FCSTD DOCUMENT  (FreeCAD 0.16R6712 (Git))
Label: UP Dose Halter
License: All rights reserved
LicenseURL: http://en.wikipedia.org/wiki/All_rights_reserved
objects: Sketcher::SketchObject×1
note: 1 computed .brp shape members not serialized (recipe doc carries the construction recipe); baked Part::Feature solids carry a one-line shape summary decoded from their .brp

FEATURE [Sketcher::SketchObject] Sketch
  sketch-geometry (39):
    g0: LineSegment StartX=7.03221 StartY=75.7575 StartZ=0 EndX=7.03221 EndY=69.7575 EndZ=0
    g1: LineSegment [constr] StartX=15.0322 StartY=67.7575 StartZ=0 EndX=15.0322 EndY=42.7575 EndZ=0
    g2: ArcOfCircle CenterX=15.0322 CenterY=42.7575 CenterZ=0 NormalX=0 NormalY=0 NormalZ=1 Radius=32 StartAngle=1.47063 EndAngle=1.67096
    g3: ArcOfCircle CenterX=15.0322 CenterY=42.7575 CenterZ=0 NormalX=0 NormalY=0 NormalZ=1 Radius=28 StartAngle=1.47063 EndAngle=1.67096
    g4: ArcOfCircle CenterX=18.0322 CenterY=72.6071 CenterZ=0 NormalX=0 NormalY=0 NormalZ=1 Radius=2 StartAngle=4.61222 EndAngle=7.75382
    g5: ArcOfCircle CenterX=12.0322 CenterY=72.6071 CenterZ=0 NormalX=0 NormalY=0 NormalZ=1 Radius=2 StartAngle=1.67096 EndAngle=4.81256
    g6: LineSegment [constr] StartX=18.0322 StartY=65.7575 StartZ=0 EndX=18.0322 EndY=72.6071 EndZ=0
    g7: ArcOfCircle CenterX=15.0322 CenterY=42.7575 CenterZ=0 NormalX=0 NormalY=0 NormalZ=1 Radius=32 StartAngle=4.61222 EndAngle=4.81256
    g8: ArcOfCircle CenterX=15.0322 CenterY=42.7575 CenterZ=0 NormalX=0 NormalY=0 NormalZ=1 Radius=28 StartAngle=4.61222 EndAngle=4.81256
    g9: ArcOfCircle CenterX=12.0322 CenterY=12.9079 CenterZ=0 NormalX=0 NormalY=0 NormalZ=1 Radius=2 StartAngle=1.47063 EndAngle=4.61222
    g10: ArcOfCircle CenterX=18.0322 CenterY=12.9079 CenterZ=0 NormalX=0 NormalY=0 NormalZ=1 Radius=2 StartAngle=4.81255 EndAngle=7.95415
    g11: ArcOfCircle CenterX=21.0322 CenterY=15.7575 CenterZ=0 NormalX=0 NormalY=0 NormalZ=1 Radius=2 StartAngle=6.28318 EndAngle=7.85398
    g12: LineSegment StartX=23.0322 StartY=15.7575 StartZ=0 EndX=23.0322 EndY=9.75753 EndZ=0
    g13: ArcOfCircle CenterX=21.0322 CenterY=9.75752 CenterZ=0 NormalX=0 NormalY=0 NormalZ=1 Radius=2 StartAngle=4.71239 EndAngle=6.28319
    g14: LineSegment StartX=7.03221 StartY=15.7575 StartZ=0 EndX=7.03221 EndY=9.75753 EndZ=0
    g15: ArcOfCircle CenterX=9.03221 CenterY=9.75752 CenterZ=0 NormalX=0 NormalY=0 NormalZ=1 Radius=2 StartAngle=3.14159 EndAngle=4.71239
    g16: LineSegment StartX=9.03221 StartY=7.75752 StartZ=0 EndX=21.0322 EndY=7.75752 EndZ=0
    g17: ArcOfCircle CenterX=9.03221 CenterY=15.7575 CenterZ=0 NormalX=0 NormalY=0 NormalZ=1 Radius=2 StartAngle=1.5708 EndAngle=3.14159
    g18: LineSegment StartX=12.0322 StartY=19.7575 StartZ=0 EndX=12.0322 EndY=65.7575 EndZ=0
    g19: ArcOfCircle CenterX=10.0322 CenterY=19.7575 CenterZ=0 NormalX=0 NormalY=0 NormalZ=1 Radius=2 StartAngle=4.71239 EndAngle=6.28319
    g20: LineSegment StartX=9.03221 StartY=17.7575 StartZ=0 EndX=10.0322 EndY=17.7575 EndZ=0
    g21: LineSegment StartX=18.0322 StartY=65.7575 StartZ=0 EndX=18.0322 EndY=19.7575 EndZ=0
    g22: ArcOfCircle CenterX=20.0322 CenterY=19.7575 CenterZ=0 NormalX=0 NormalY=0 NormalZ=1 Radius=2 StartAngle=3.14159 EndAngle=4.71239
    g23: LineSegment StartX=20.0322 StartY=17.7575 StartZ=0 EndX=21.0322 EndY=17.7575 EndZ=0
    g24: LineSegment [constr] StartX=18.0322 StartY=19.7575 StartZ=0 EndX=18.0322 EndY=12.9079 EndZ=0
    g25: ArcOfCircle CenterX=20.0322 CenterY=65.7575 CenterZ=0 NormalX=0 NormalY=0 NormalZ=1 Radius=2 StartAngle=1.5708 EndAngle=3.14159
    g26: ArcOfCircle CenterX=21.0322 CenterY=69.7575 CenterZ=0 NormalX=0 NormalY=0 NormalZ=1 Radius=2 StartAngle=4.71239 EndAngle=6.28319
    g27: LineSegment StartX=20.0322 StartY=67.7575 StartZ=0 EndX=21.0322 EndY=67.7575 EndZ=0
    g28: ArcOfCircle CenterX=21.0322 CenterY=75.7575 CenterZ=0 NormalX=0 NormalY=0 NormalZ=1 Radius=2 StartAngle=6.28318 EndAngle=7.85398
    g29: LineSegment StartX=23.0322 StartY=75.7575 StartZ=0 EndX=23.0322 EndY=69.7575 EndZ=0
    g30: ArcOfCircle CenterX=9.03221 CenterY=75.7575 CenterZ=0 NormalX=0 NormalY=0 NormalZ=1 Radius=2 StartAngle=1.5708 EndAngle=3.14159
    g31: LineSegment StartX=9.0322 StartY=77.7575 StartZ=0 EndX=21.0322 EndY=77.7575 EndZ=0
    g32: ArcOfCircle CenterX=9.03221 CenterY=69.7575 CenterZ=0 NormalX=0 NormalY=0 NormalZ=1 Radius=2 StartAngle=3.14159 EndAngle=4.71238
    g33: ArcOfCircle CenterX=10.0322 CenterY=65.7575 CenterZ=0 NormalX=0 NormalY=0 NormalZ=1 Radius=2 StartAngle=6.28318 EndAngle=7.85398
    g34: LineSegment StartX=9.0322 StartY=67.7575 StartZ=0 EndX=10.0322 EndY=67.7575 EndZ=0
    g35: LineSegment [constr] StartX=10.0322 StartY=67.7575 StartZ=0 EndX=15.0322 EndY=67.7575 EndZ=0
    g36: LineSegment [constr] StartX=12.0322 StartY=65.7575 StartZ=0 EndX=15.0322 EndY=65.7575 EndZ=0
    g37: Circle CenterX=15.0322 CenterY=58.7575 CenterZ=0 NormalX=0 NormalY=0 NormalZ=1 Radius=1.2
    g38: Circle CenterX=15.0322 CenterY=26.7575 CenterZ=0 NormalX=0 NormalY=0 NormalZ=1 Radius=1.2
  constraints (125):
    c: Vertical(g0)
    c: Vertical(g1)
    c: DistanceY(g1,g1) = 25
    c: Coincident(g2,g1)
    c: Radius(g2) = 32
    c: Coincident(g3,g1)
    c: Radius(g3) = 28
    c: Coincident(g4,g2)
    c: Coincident(g4,g3)
    c: Radius(g4) = 2
    c: Coincident(g5,g2)
    c: Coincident(g5,g3)
    c: Radius(g5) = 2
    c: DistanceX(g5,g4) = 6
    c: Coincident(g6,g4)
    c: Vertical(g6)
    c: Coincident(g7,g1)
    c: Radius(g8) = 28
    c: Radius(g7) = 32
    c: Coincident(g9,g8)
    c: Coincident(g9,g7)
    c: Coincident(g10,g8)
    c: Coincident(g10,g7)
    c: Radius(g10) = 2
    c: Equal(g10,g9)
    c: DistanceX(g9,g10) = 6
    c: Coincident(g8,g1)
    c: Vertical(g12)
    c: Vertical(g14)
    c: Coincident(g16,g15)
    c: Coincident(g12,g13)
    c: Tangent(g12,g13)
    c: Coincident(g11,g12)
    c: Horizontal(g16)
    c: Coincident(g16,g13)
    c: Tangent(g16,g15)
    c: Tangent(g14,g15)
    c: Coincident(g15,g14)
    c: Coincident(g17,g14)
    c: Tangent(g14,g17)
    c: Vertical(g18)
    c: Coincident(g19,g18)
    c: Coincident(g20,g17)
    c: Coincident(g20,g19)
    c: Horizontal(g20)
    c: Tangent(g19,g20)
    c: Tangent(g19,g18)
    c: Vertical(g21)
    c: Coincident(g22,g21)
    c: Tangent(g22,g21)
    c: Coincident(g23,g22)
    c: Horizontal(g23)
    c: Tangent(g23,g11)
    c: Tangent(g22,g23)
    c: Coincident(g24,g21)
    c: Coincident(g24,g10)
    c: Vertical(g24)
    c: DistanceX(g14,g12) = 16
    c: DistanceY(g13,g11) = 10
    c: Tangent(g12,g11)
    c: Coincident(g11,g23)
    c: Equal(g23,g20)
    c: Tangent(g17,g20)
    c: Radius(g17) = 2
    c: Equal(g17,g19)
    c: Equal(g17,g22)
    c: Equal(g17,g11)
    c: Equal(g17,g13)
    c: Equal(g17,g15)
    c: DistanceY(g15,g17) = 10
    c: DistanceX(g18,g21) = 6
    c: Coincident(g25,g21)
    c: Coincident(g27,g25)
    c: Coincident(g27,g26)
    c: Coincident(g29,g26)
    c: Coincident(g28,g29)
    c: Tangent(g21,g25)
    c: Tangent(g27,g25)
    c: Horizontal(g27)
    c: Tangent(g26,g27)
    c: Tangent(g29,g26)
    c: Tangent(g28,g29)
    c: Coincident(g30,g0)
    c: Coincident(g31,g30)
    c: Coincident(g31,g28)
    c: Horizontal(g31)
    c: Tangent(g30,g31)
    c: Tangent(g0,g30)
    c: Coincident(g34,g33)
    c: Coincident(g33,g18)
    c: Tangent(g18,g33)
    c: Tangent(g33,g34)
    c: Tangent(g32,g34)
    c: Tangent(g0,g32)
    c: Coincident(g0,g32)
    c: Coincident(g32,g34)
    c: Horizontal(g34)
    c: DistanceY(g11,g26) = 50
    c: Equal(g33,g32)
    c: Equal(g32,g30)
    c: Equal(g30,g28)
    c: Equal(g28,g26)
    c: Equal(g26,g25)
    c: Equal(g25,g17)
    c: Tangent(g31,g28)
    c: Vertical(g29)
    c: DistanceY(g26,g28) = 10
    c: Equal(g27,g34)
    c: DistanceY(g32,g30) = 10
    c: Coincident(g6,g21)
    c: Coincident(g35,g33)
    c: Coincident(g35,g1)
    c: Horizontal(g35)
    c: Coincident(g36,g18)
    c: PointOnObject(g36,g1)
    c: Horizontal(g36)
    c: DistanceX(g36,g36) = 3
    c: DistanceX(g0,g28) = 16
    c: Radius(g37) = 1.2
    c: DistanceY(g1,g37) = 16
    c: DistanceX(g37,g1) = 0
    c: Equal(g38,g37)
    c: DistanceY(g38,g1) = 16
    c: DistanceX(g38,g1) = 0
    c: Tangent(g16,g13)
